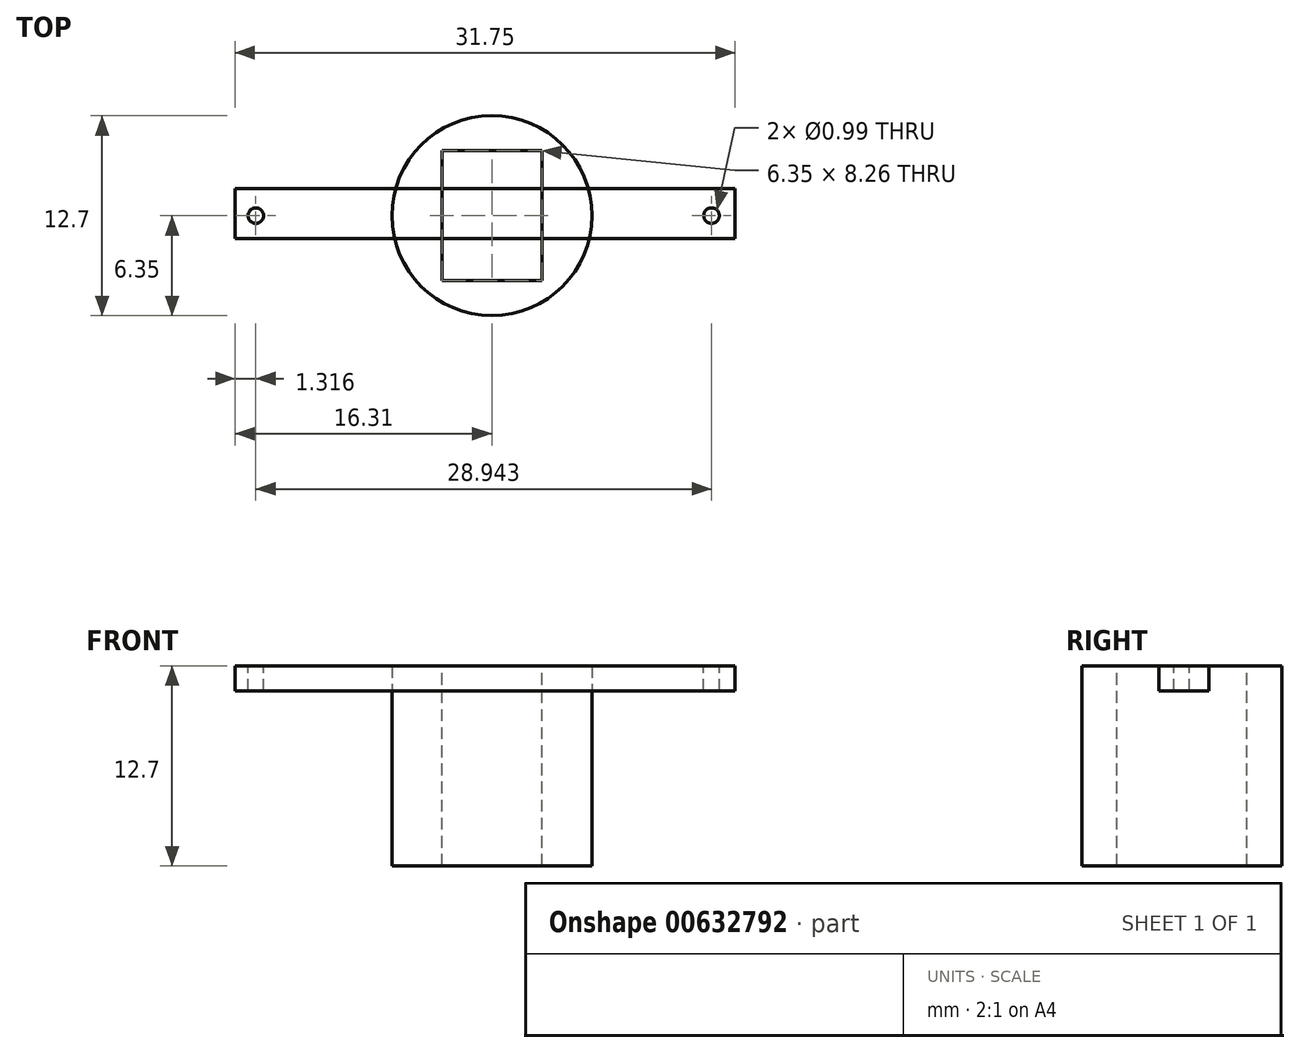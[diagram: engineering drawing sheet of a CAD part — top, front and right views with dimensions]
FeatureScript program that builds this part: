
annotation { "Feature Type Name" : "Feature", "Feature Type Description" : "" }
export const myFeature = defineFeature(function(context is Context, id is Id, definition is map)
    precondition{}
    {
        {
            var Q0;
            Q0=qCreatedBy(makeId("Top.planeOp"),FACE);
            var sketch = newSketch(context, id + "F0", { "sketchPlane" : qUnion([Q0])});
            skCircle(sketch, "E0", {"center": v(0, 0) * mm, "radius": 6.35 * mm});
            skSolve(sketch);
        }
        {
            var Q0;
            Q0=makeQuery(id+"F0.imprint","IMPRINT",FACE,{"disambiguationData":[TD([[makeQuery(id+"F0.imprint","IMPRINT",EDGE,{"derivedFrom":sQuery(id+"F0.wireOp",EDGE,"E0")}),1.0]])]});
            extrude(context, id + "F1", {"entities" : qUnion([Q0]), "depth" : 12.7 * mm, "offsetDistance" : 25.4 * mm});
        }
        {
            var Q0;
            Q0=makeQuery(id+"F1.opExtrude","CAP_FACE",FACE,{"disambiguationData":[OSD([sQuery(id+"F0.wireOp",EDGE,"E0")])],"isStart":false});
            var sketch = newSketch(context, id + "F2", { "sketchPlane" : qUnion([Q0])});
            skLineSegment(sketch, "E1.bottom", {"start": v(3.18, -4.13) * mm, "end": v(-3.17, -4.13) * mm});
            skLineSegment(sketch, "E1.top", {"start": v(3.17, 4.13) * mm, "end": v(-3.18, 4.13) * mm});
            skLineSegment(sketch, "E1.left", {"start": v(3.18, -4.13) * mm, "end": v(3.17, 4.13) * mm});
            skLineSegment(sketch, "E1.right", {"start": v(-3.17, -4.13) * mm, "end": v(-3.18, 4.13) * mm});
            skPoint(sketch, "E1.middle", {"position": v(0, 0) * mm});
            skSolve(sketch);
        }
        {
            var Q0;
            Q0=makeQuery(id+"F2.imprint","IMPRINT",FACE,{"disambiguationData":[TD([[makeQuery(id+"F2.imprint","IMPRINT",EDGE,{"derivedFrom":sQuery(id+"F2.wireOp",EDGE,"E1.bottom")}),-1.0]])]});
            extrude(context, id + "F3", {"entities" : qUnion([Q0]), "operationType" : NewBodyOperationType.REMOVE, "oppositeDirection" : true, "depth" : 25.4 * mm, "offsetDistance" : 25.4 * mm});
        }
        {
            var Q0;
            Q0=makeQuery(id+"F1.opExtrude","CAP_FACE",FACE,{"disambiguationData":[OSD([sQuery(id+"F0.wireOp",EDGE,"E0")])],"isStart":false});
            var sketch = newSketch(context, id + "F4", { "sketchPlane" : qUnion([Q0])});
            skLineSegment(sketch, "E2.bottom", {"start": v(15.44, -1.47) * mm, "end": v(-16.31, -1.47) * mm});
            skLineSegment(sketch, "E2.top", {"start": v(15.44, 1.7) * mm, "end": v(-16.31, 1.7) * mm});
            skLineSegment(sketch, "E2.left", {"start": v(15.44, -1.47) * mm, "end": v(15.44, 1.7) * mm});
            skLineSegment(sketch, "E2.right", {"start": v(-16.31, -1.47) * mm, "end": v(-16.31, 1.7) * mm});
            skSolve(sketch);
        }
        {
            var Q0;
            Q0 = qSketchRegion(id + "F4", true);
            extrude(context, id + "F5", {"entities" : qUnion([Q0]), "depth" : -1.59 * mm, "offsetDistance" : 25.4 * mm});
        }
        {
            var Q0;
            Q0=makeQuery(id+"F5.opExtrude","CAP_FACE",FACE,{"disambiguationData":[OSD([sQuery(id+"F4.wireOp",EDGE,"E2.bottom"),sQuery(id+"F4.wireOp",EDGE,"E2.top"),sQuery(id+"F4.wireOp",EDGE,"E2.left"),sQuery(id+"F4.wireOp",EDGE,"E2.right")])],"isStart":true});
            var sketch = newSketch(context, id + "F6", { "sketchPlane" : qUnion([Q0])});
            skCircle(sketch, "E3", {"center": v(13.95, 0) * mm, "radius": 0.5 * mm});
            skSolve(sketch);
        }
        {
            var Q0;
            Q0=makeQuery(id+"F6.imprint","IMPRINT",FACE,{"disambiguationData":[TD([[makeQuery(id+"F6.imprint","IMPRINT",EDGE,{"derivedFrom":sQuery(id+"F6.wireOp",EDGE,"E3")}),1.0]])]});
            var Q1;
            Q1=sQuery(id+"F6.wireOp",EDGE,"E3");
            extrude(context, id + "F7", {"entities" : qUnion([Q0]), "operationType" : NewBodyOperationType.REMOVE, "surfaceEntities" : qUnion([Q1]), "oppositeDirection" : true, "depth" : 1.59 * mm, "offsetDistance" : 25.4 * mm});
        }
        {
            var Q0;
            Q0=makeQuery(id+"F5.opExtrude","CAP_FACE",FACE,{"disambiguationData":[OSD([sQuery(id+"F4.wireOp",EDGE,"E2.bottom"),sQuery(id+"F4.wireOp",EDGE,"E2.top"),sQuery(id+"F4.wireOp",EDGE,"E2.left"),sQuery(id+"F4.wireOp",EDGE,"E2.right")])],"isStart":true});
            var sketch = newSketch(context, id + "F8", { "sketchPlane" : qUnion([Q0])});
            skLineSegment(sketch, "E4", {"start": v(6.37, 0) * mm, "end": v(15.44, 0) * mm});
            skSolve(sketch);
        }
        {
            var Q0;
            {var subQ1=makeQuery(id+"F5.opExtrude","CAP_EDGE",EDGE,{"disambiguationData":[OSD([sQuery(id+"F4.wireOp",EDGE,"E2.bottom")])],"isStart":true});Q0=makeQuery(id+"F8.imprint","IMPRINT",FACE,{"disambiguationData":[TD([[makeQuery(id+"F8.imprint","IMPRINT",EDGE,{"derivedFrom":subQ1}),-1.0]])]});}
            var sketch = newSketch(context, id + "F9", { "sketchPlane" : qUnion([Q0])});
            skCircle(sketch, "E5", {"center": v(-15, 0) * mm, "radius": 0.5 * mm});
            skSolve(sketch);
        }
        {
            var Q0;
            Q0 = qSketchRegion(id + "F9", true);
            extrude(context, id + "F10", {"entities" : qUnion([Q0]), "operationType" : NewBodyOperationType.REMOVE, "oppositeDirection" : true, "depth" : 25.4 * mm, "offsetDistance" : 25.4 * mm});
        }
    });
